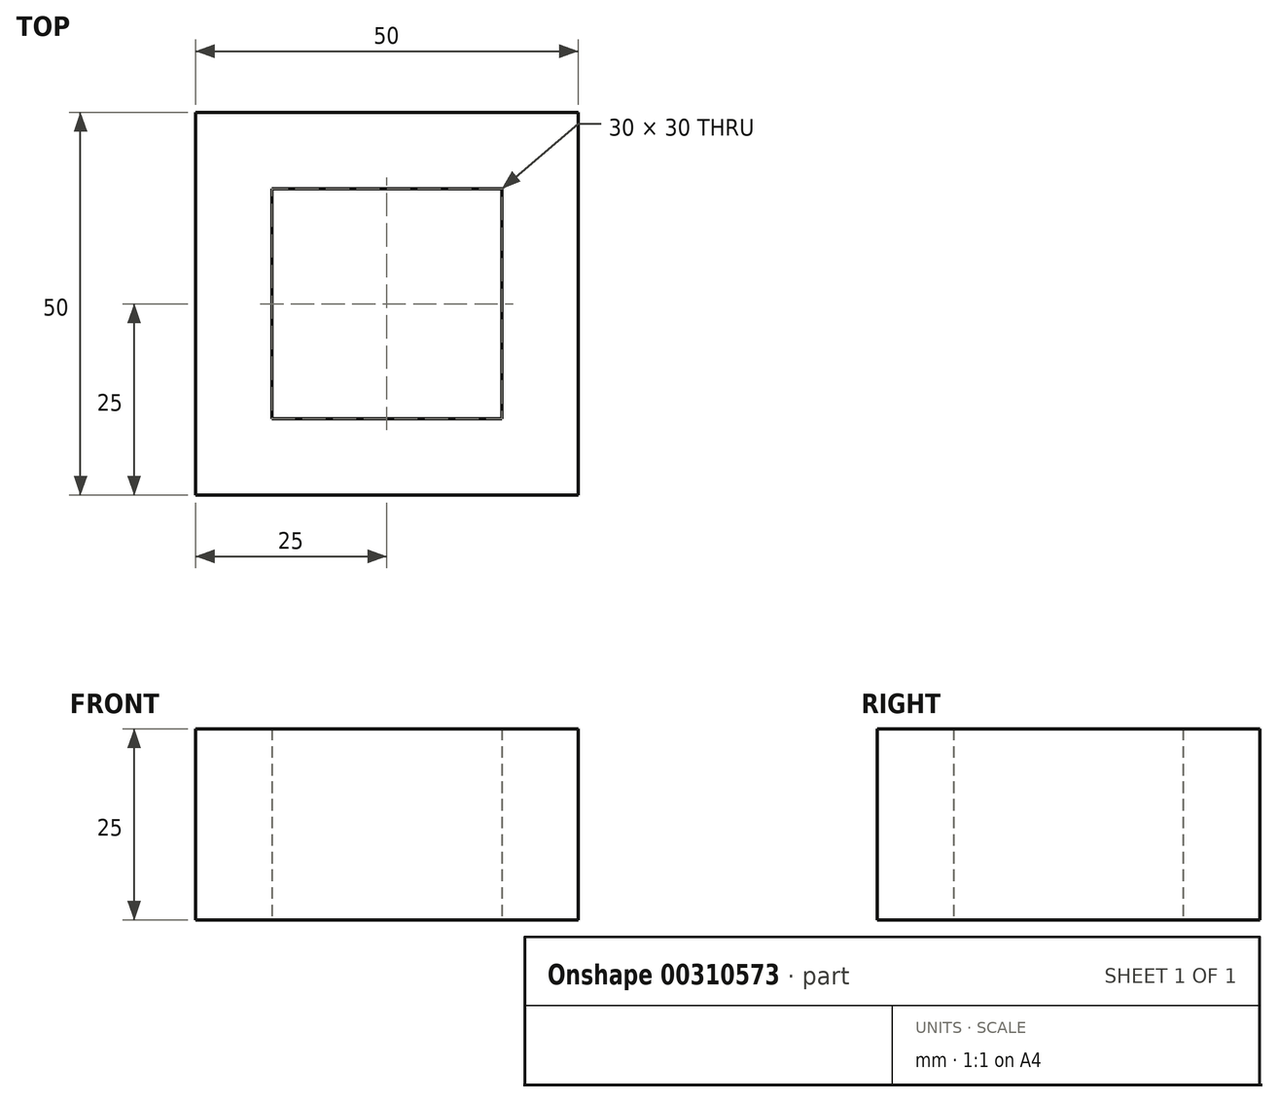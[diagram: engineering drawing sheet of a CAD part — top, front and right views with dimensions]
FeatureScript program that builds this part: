
annotation { "Feature Type Name" : "Feature", "Feature Type Description" : "" }
export const myFeature = defineFeature(function(context is Context, id is Id, definition is map)
    precondition{}
    {
        {
            var Q0;
            Q0=qCreatedBy(makeId("Top.planeOp"),FACE);
            var sketch = newSketch(context, id + "F0", { "sketchPlane" : qUnion([Q0])});
            skLineSegment(sketch, "E0.bottom", {"start": v(0, 0) * mm, "end": v(-50, 0) * mm});
            skLineSegment(sketch, "E0.top", {"start": v(0, 50) * mm, "end": v(-50, 50) * mm});
            skLineSegment(sketch, "E0.left", {"start": v(0, 0) * mm, "end": v(0, 50) * mm});
            skLineSegment(sketch, "E0.right", {"start": v(-50, 0) * mm, "end": v(-50, 50) * mm});
            skLineSegment(sketch, "E1.bottom", {"start": v(0, 0) * mm, "end": v(-10, 0) * mm});
            skLineSegment(sketch, "E1.left", {"start": v(0, 0) * mm, "end": v(0, 10) * mm});
            skLineSegment(sketch, "E2.bottom", {"start": v(-10, 10) * mm, "end": v(-40, 10) * mm});
            skLineSegment(sketch, "E2.top", {"start": v(-10, 40) * mm, "end": v(-40, 40) * mm});
            skLineSegment(sketch, "E2.left", {"start": v(-10, 10) * mm, "end": v(-10, 40) * mm});
            skLineSegment(sketch, "E2.right", {"start": v(-40, 10) * mm, "end": v(-40, 40) * mm});
            skSolve(sketch);
        }
        {
            var Q0;
            Q0=makeQuery(id+"F0.imprint","IMPRINT",FACE,{"disambiguationData":[TD([[makeQuery(id+"F0.imprint","IMPRINT",EDGE,{"derivedFrom":sQuery(id+"F0.wireOp",EDGE,"E0.bottom")}),-1.0]])]});
            extrude(context, id + "F1", {"entities" : qUnion([Q0]), "depth" : 25 * mm});
        }
    });
